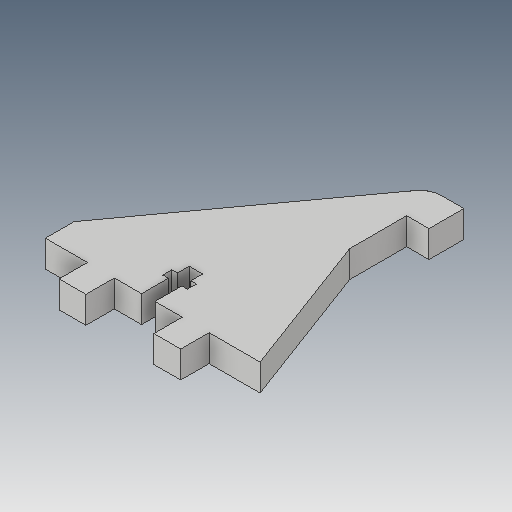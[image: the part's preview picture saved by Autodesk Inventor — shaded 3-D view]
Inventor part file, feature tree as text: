
AUTODESK INVENTOR PART (.ipt)
format: ipt  version: 2017 (Build 210142000, 142)  size: 131,072 bytes
history: native  units: mm
features: extrude x1, sketch x1
ambient origin geometry x8: Origin, YZ Plane, XZ Plane, XY Plane, X Axis, Y Axis, Z Axis, Center Point
bodies: Solid1 (feature_tree)
feature tree (2):
  extrude  "Extrusion1"  [1 undecoded]
  sketch  "Sketch1"  dims[d0=6.0mm d1=0.0mm]
note: 1 required parameter value undecoded (feature->parameter linkage not recoverable at this tier; creation-order binding heuristic only, values carry confidence <= 0.55)
